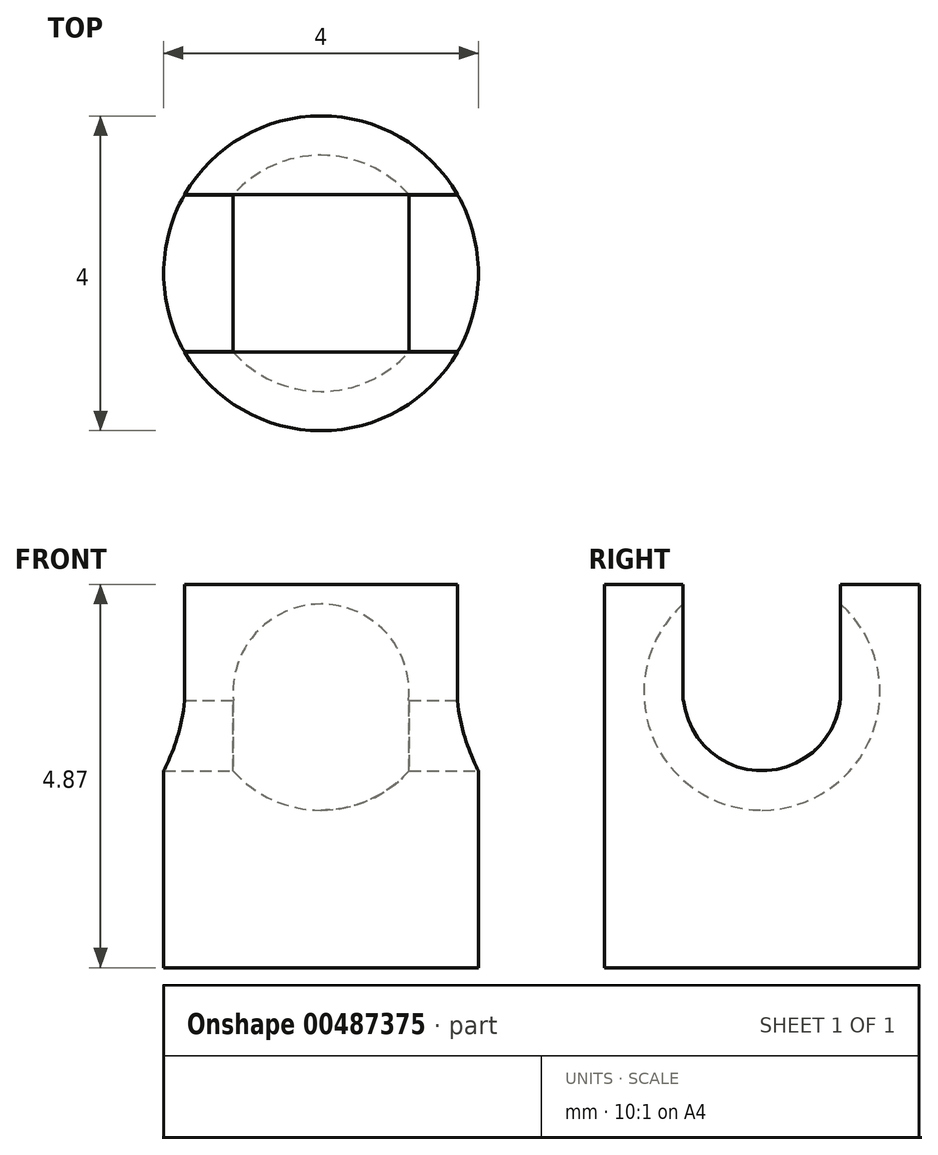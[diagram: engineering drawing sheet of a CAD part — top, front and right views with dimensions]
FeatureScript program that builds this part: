
annotation { "Feature Type Name" : "Feature", "Feature Type Description" : "" }
export const myFeature = defineFeature(function(context is Context, id is Id, definition is map)
    precondition{}
    {
        {
            var Q0;
            Q0=qCreatedBy(makeId("Top.planeOp"),FACE);
            var sketch = newSketch(context, id + "F0", { "sketchPlane" : qUnion([Q0])});
            skCircle(sketch, "E0", {"center": v(0, 0) * mm, "radius": 2 * mm});
            skSolve(sketch);
        }
        {
            var Q0;
            Q0 = qSketchRegion(id + "F0", true);
            extrude(context, id + "F1", {"entities" : qUnion([Q0]), "depth" : 6 * mm});
        }
        {
            var Q0;
            Q0=qCreatedBy(makeId("Right.planeOp"),FACE);
            var sketch = newSketch(context, id + "F2", { "sketchPlane" : qUnion([Q0])});
            skCircle(sketch, "E1", {"center": v(0, 3.5) * mm, "radius": 1 * mm});
            skSolve(sketch);
        }
        {
            var Q0;
            Q0 = qSketchRegion(id + "F2", true);
            extrude(context, id + "F3", {"entities" : qUnion([Q0]), "operationType" : NewBodyOperationType.REMOVE, "endBound" : BoundingType.SYMMETRIC, "oppositeDirection" : true, "depth" : 25 * mm});
        }
        {
            var Q0;
            Q0=qCreatedBy(makeId("Right.planeOp"),FACE);
            var sketch = newSketch(context, id + "F4", { "sketchPlane" : qUnion([Q0])});
            skLineSegment(sketch, "E2", {"start": v(1, 3.4) * mm, "end": v(1, 8.36) * mm});
            skLineSegment(sketch, "E3", {"start": v(1, 8.36) * mm, "end": v(-1, 8.36) * mm});
            skLineSegment(sketch, "E4", {"start": v(-1, 8.36) * mm, "end": v(-1, 3.4) * mm});
            skLineSegment(sketch, "E5", {"start": v(-1, 3.4) * mm, "end": v(1, 3.4) * mm});
            skSolve(sketch);
        }
        {
            var Q0;
            Q0 = qSketchRegion(id + "F4", true);
            extrude(context, id + "F5", {"entities" : qUnion([Q0]), "operationType" : NewBodyOperationType.REMOVE, "endBound" : BoundingType.SYMMETRIC, "oppositeDirection" : true, "depth" : 25 * mm});
        }
        {
            var Q0;
            Q0=qCreatedBy(makeId("Front.planeOp"),FACE);
            var sketch = newSketch(context, id + "F6", { "sketchPlane" : qUnion([Q0])});
            skArc(sketch, "E6", {"start": v(0, 5) * mm, "mid": v(-1.5, 3.5) * mm, "end": v(0, 2) * mm});
            skLineSegment(sketch, "E7", {"start": v(0, 5) * mm, "end": v(0, 2) * mm});
            skSolve(sketch);
        }
        {
            var Q0;
            Q0 = qSketchRegion(id + "F6", true);
            var Q1;
            Q1=sQuery(id+"F6.wireOp",EDGE,"E7");
            revolve(context, id + "F7", {"operationType" : NewBodyOperationType.REMOVE, "entities" : qUnion([Q0]), "axis" : qUnion([Q1]), "revolveType" : RevolveType.FULL, "oppositeDirection" : true});
        }
        {
            var Q0;
            Q0=qCreatedBy(makeId("Right.planeOp"),FACE);
            var sketch = newSketch(context, id + "F8", { "sketchPlane" : qUnion([Q0])});
            skLineSegment(sketch, "E8.bottom", {"start": v(-5.38, 7.28) * mm, "end": v(6.87, 7.28) * mm});
            skLineSegment(sketch, "E8.top", {"start": v(-5.38, 4.87) * mm, "end": v(6.87, 4.87) * mm});
            skLineSegment(sketch, "E8.left", {"start": v(-5.38, 7.28) * mm, "end": v(-5.38, 4.87) * mm});
            skLineSegment(sketch, "E8.right", {"start": v(6.87, 7.28) * mm, "end": v(6.87, 4.87) * mm});
            skSolve(sketch);
        }
        {
            var Q0;
            Q0 = qSketchRegion(id + "F8", true);
            extrude(context, id + "F9", {"entities" : qUnion([Q0]), "operationType" : NewBodyOperationType.REMOVE, "endBound" : BoundingType.SYMMETRIC, "oppositeDirection" : true, "depth" : 25 * mm});
        }
    });
